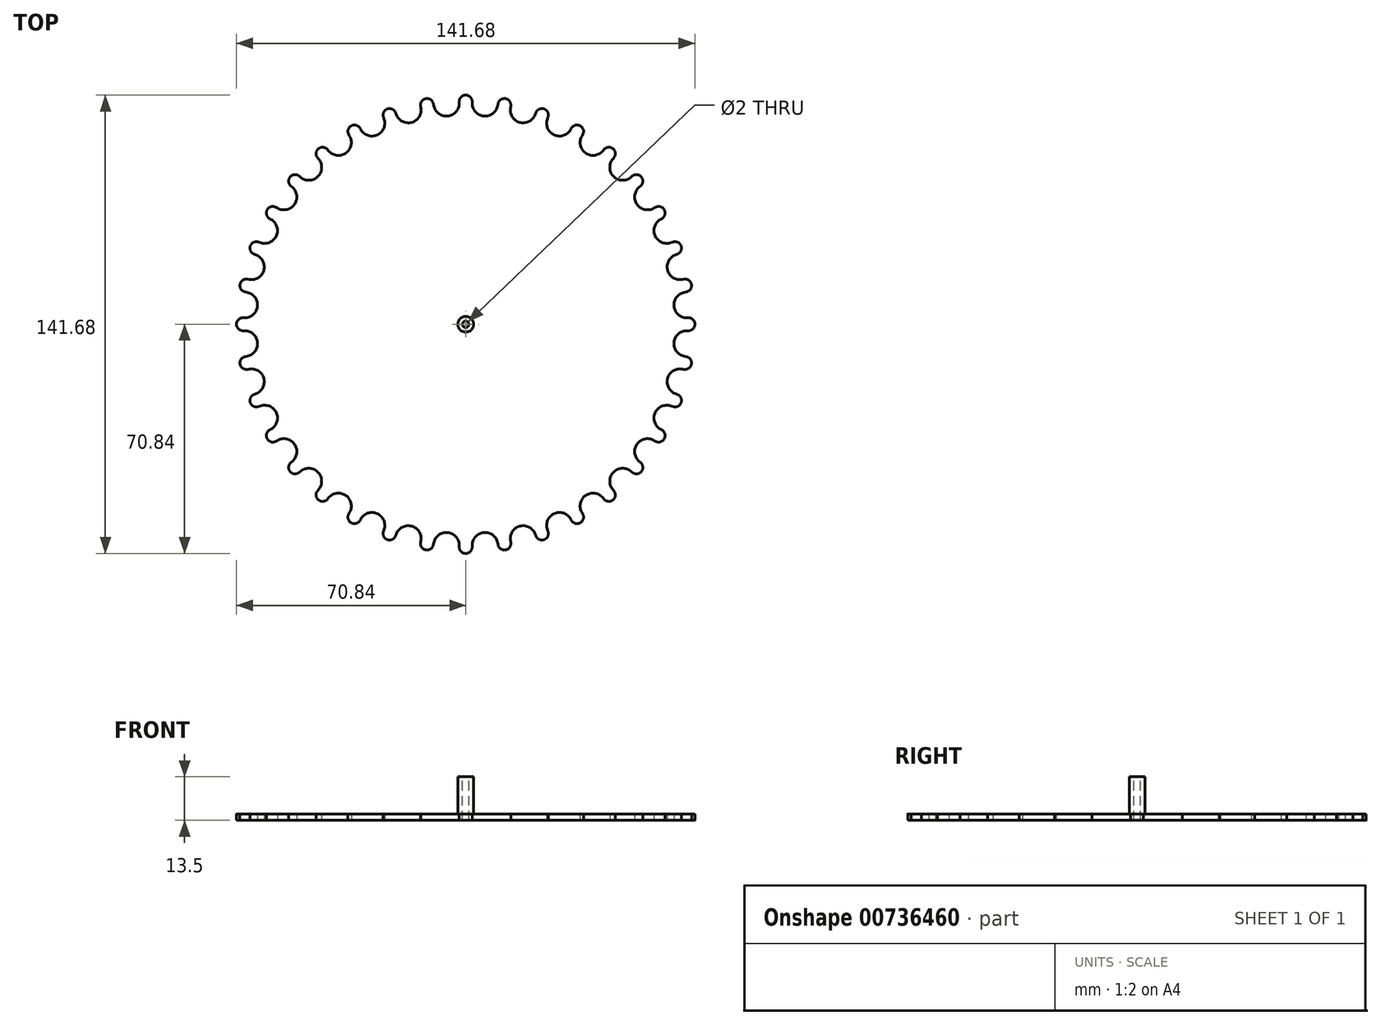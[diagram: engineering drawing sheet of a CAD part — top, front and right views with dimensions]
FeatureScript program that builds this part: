
annotation { "Feature Type Name" : "Feature", "Feature Type Description" : "" }
export const myFeature = defineFeature(function(context is Context, id is Id, definition is map)
    precondition{}
    {
        {
            var Q0;
            Q0=qCreatedBy(makeId("Top.planeOp"),FACE);
            var sketch = newSketch(context, id + "F0", { "sketchPlane" : qUnion([Q0])});
            skArc(sketch, "E0", {"start": v(2, 68.84) * mm, "mid": v(0, 70.84) * mm, "end": v(-2, 68.84) * mm});
            skLineSegment(sketch, "E1", {"start": v(2, 68.84) * mm, "end": v(2, 68.32) * mm});
            skLineSegment(sketch, "E2", {"start": v(-2, 68.84) * mm, "end": v(-2, 68.32) * mm});
            skLineSegment(sketch, "E3", {"start": v(-5.98, 68.32) * mm, "end": v(-5.63, 64.36) * mm, "construction": true});
            skArc(sketch, "E4", {"start": v(-5.63, 64.36) * mm, "mid": v(-3.04, 65.63) * mm, "end": v(-2, 68.32) * mm});
            skLineSegment(sketch, "E5", {"start": v(-5.63, 64.36) * mm, "end": v(-4.63, 64.44) * mm, "construction": true});
            skLineSegment(sketch, "E6", {"start": v(0, 0) * mm, "end": v(-5.63, 64.36) * mm});
            skArc(sketch, "E7", {"start": v(2, 68.32) * mm, "mid": v(3.04, 65.63) * mm, "end": v(5.63, 64.36) * mm});
            skLineSegment(sketch, "E8", {"start": v(5.98, 68.32) * mm, "end": v(5.63, 64.36) * mm, "construction": true});
            skLineSegment(sketch, "E9", {"start": v(5.63, 64.36) * mm, "end": v(4.63, 64.44) * mm, "construction": true});
            skLineSegment(sketch, "E10", {"start": v(0, 0) * mm, "end": v(5.63, 64.36) * mm});
            skCircle(sketch, "E11.cCircle", {"center": v(0, 0) * mm, "radius": 68.84 * mm, "construction": true});
            skLineSegment(sketch, "E11.0", {"start": v(0, 68.84) * mm, "end": v(11.95, 67.8) * mm, "construction": true});
            skLineSegment(sketch, "E11.1", {"start": v(11.95, 67.8) * mm, "end": v(23.55, 64.7) * mm, "construction": true});
            skLineSegment(sketch, "E11.2", {"start": v(23.55, 64.7) * mm, "end": v(34.42, 59.62) * mm, "construction": true});
            skLineSegment(sketch, "E11.3", {"start": v(34.42, 59.62) * mm, "end": v(44.25, 52.74) * mm, "construction": true});
            skLineSegment(sketch, "E11.4", {"start": v(44.25, 52.74) * mm, "end": v(52.74, 44.25) * mm, "construction": true});
            skLineSegment(sketch, "E11.5", {"start": v(52.74, 44.25) * mm, "end": v(59.62, 34.42) * mm, "construction": true});
            skLineSegment(sketch, "E11.6", {"start": v(59.62, 34.42) * mm, "end": v(64.7, 23.55) * mm, "construction": true});
            skLineSegment(sketch, "E11.7", {"start": v(64.7, 23.55) * mm, "end": v(67.8, 11.95) * mm, "construction": true});
            skLineSegment(sketch, "E11.8", {"start": v(67.8, 11.95) * mm, "end": v(68.84, 0) * mm, "construction": true});
            skLineSegment(sketch, "E11.9", {"start": v(68.84, 0) * mm, "end": v(67.8, -11.95) * mm, "construction": true});
            skLineSegment(sketch, "E11.10", {"start": v(67.8, -11.95) * mm, "end": v(64.7, -23.55) * mm, "construction": true});
            skLineSegment(sketch, "E11.11", {"start": v(64.7, -23.55) * mm, "end": v(59.62, -34.42) * mm, "construction": true});
            skLineSegment(sketch, "E11.12", {"start": v(59.62, -34.42) * mm, "end": v(52.74, -44.25) * mm, "construction": true});
            skLineSegment(sketch, "E11.13", {"start": v(52.74, -44.25) * mm, "end": v(44.25, -52.74) * mm, "construction": true});
            skLineSegment(sketch, "E11.14", {"start": v(44.25, -52.74) * mm, "end": v(34.42, -59.62) * mm, "construction": true});
            skLineSegment(sketch, "E11.15", {"start": v(34.42, -59.62) * mm, "end": v(23.55, -64.7) * mm, "construction": true});
            skLineSegment(sketch, "E11.16", {"start": v(23.55, -64.7) * mm, "end": v(11.95, -67.8) * mm, "construction": true});
            skLineSegment(sketch, "E11.17", {"start": v(11.95, -67.8) * mm, "end": v(0, -68.84) * mm, "construction": true});
            skLineSegment(sketch, "E11.18", {"start": v(0, -68.84) * mm, "end": v(-11.95, -67.8) * mm, "construction": true});
            skLineSegment(sketch, "E11.19", {"start": v(-11.95, -67.8) * mm, "end": v(-23.55, -64.7) * mm, "construction": true});
            skLineSegment(sketch, "E11.20", {"start": v(-23.55, -64.7) * mm, "end": v(-34.42, -59.62) * mm, "construction": true});
            skLineSegment(sketch, "E11.21", {"start": v(-34.42, -59.62) * mm, "end": v(-44.25, -52.74) * mm, "construction": true});
            skLineSegment(sketch, "E11.22", {"start": v(-44.25, -52.74) * mm, "end": v(-52.74, -44.25) * mm, "construction": true});
            skLineSegment(sketch, "E11.23", {"start": v(-52.74, -44.25) * mm, "end": v(-59.62, -34.42) * mm, "construction": true});
            skLineSegment(sketch, "E11.24", {"start": v(-59.62, -34.42) * mm, "end": v(-64.7, -23.55) * mm, "construction": true});
            skLineSegment(sketch, "E11.25", {"start": v(-64.7, -23.55) * mm, "end": v(-67.8, -11.95) * mm, "construction": true});
            skLineSegment(sketch, "E11.26", {"start": v(-67.8, -11.95) * mm, "end": v(-68.84, 0) * mm, "construction": true});
            skLineSegment(sketch, "E11.27", {"start": v(-68.84, 0) * mm, "end": v(-67.8, 11.95) * mm});
            skLineSegment(sketch, "E11.28", {"start": v(-67.8, 11.95) * mm, "end": v(-64.7, 23.55) * mm, "construction": true});
            skLineSegment(sketch, "E11.29", {"start": v(-64.7, 23.55) * mm, "end": v(-59.62, 34.42) * mm, "construction": true});
            skLineSegment(sketch, "E11.30", {"start": v(-59.62, 34.42) * mm, "end": v(-52.74, 44.25) * mm, "construction": true});
            skLineSegment(sketch, "E11.31", {"start": v(-52.74, 44.25) * mm, "end": v(-44.25, 52.74) * mm, "construction": true});
            skLineSegment(sketch, "E11.32", {"start": v(-44.25, 52.74) * mm, "end": v(-34.42, 59.62) * mm, "construction": true});
            skLineSegment(sketch, "E11.33", {"start": v(-34.42, 59.62) * mm, "end": v(-23.55, 64.7) * mm, "construction": true});
            skLineSegment(sketch, "E11.34", {"start": v(-23.55, 64.7) * mm, "end": v(-11.95, 67.8) * mm, "construction": true});
            skLineSegment(sketch, "E11.35", {"start": v(-11.95, 67.8) * mm, "end": v(0, 68.84) * mm, "construction": true});
            skSolve(sketch);
        }
        {
            var Q0;
            Q0=qSketchRegion(id+"F0",true);
            extrude(context, id + "F1", {"entities" : qUnion([Q0]), "endBound" : BoundingType.SYMMETRIC, "depth" : 2 * mm, "offsetDistance" : 25 * mm});
        }
        {
            var Q0;
            Q0=makeQuery(id+"F1.opExtrude","SWEPT_BODY",BODY,{"disambiguationData":[OSD([sQuery(id+"F0.wireOp",EDGE,"E0"),sQuery(id+"F0.wireOp",EDGE,"E1"),sQuery(id+"F0.wireOp",EDGE,"E2"),sQuery(id+"F0.wireOp",EDGE,"E4"),sQuery(id+"F0.wireOp",EDGE,"W5vAHDtY-rvEH-ViCa-0FPo-8mxshjeyYw7U"),sQuery(id+"F0.wireOp",EDGE,"J2sdAHte-avJF-ZFeu-cnuh-1Djj5LRI9oCG"),sQuery(id+"F0.wireOp",EDGE,"E6")])]});
            var Q1;
            Q1=makeQuery(id+"F1.opExtrude","SWEPT_EDGE",EDGE,{"disambiguationData":[OSD([sQuery(id+"F0.wireOp",EDGE,"E6"),sQuery(id+"F0.wireOp",EDGE,"E10")])]});
            circularPattern(context, id + "F2", {"operationType" : NewBodyOperationType.ADD, "entities" : qUnion([Q0]), "axis" : qUnion([Q1]), "angle" : 360 * degree, "instanceCount" : 36, "equalSpace" : true});
        }
        {
            var Q0;
            Q0=qCreatedBy(makeId("Top.planeOp"),FACE);
            var sketch = newSketch(context, id + "F3", { "sketchPlane" : qUnion([Q0])});
            skCircle(sketch, "E12", {"center": v(0, 0) * mm, "radius": 2.4 * mm});
            skSolve(sketch);
        }
        {
            var Q0;
            Q0=qSketchRegion(id+"F3",true);
            extrude(context, id + "F4", {"entities" : qUnion([Q0]), "operationType" : NewBodyOperationType.ADD, "depth" : 12.5 * mm, "offsetDistance" : 25 * mm});
        }
        {
            var Q0;
            Q0=makeQuery(id+"F4.opExtrude","CAP_FACE",FACE,{"disambiguationData":[OSD([sQuery(id+"F3.wireOp",EDGE,"E12")])],"isStart":false});
            var sketch = newSketch(context, id + "F5", { "sketchPlane" : qUnion([Q0])});
            skCircle(sketch, "E13", {"center": v(0, 0) * mm, "radius": 1 * mm});
            skSolve(sketch);
        }
        {
            var Q0;
            Q0=qSketchRegion(id+"F5",true);
            extrude(context, id + "F6", {"entities" : qUnion([Q0]), "operationType" : NewBodyOperationType.REMOVE, "endBound" : BoundingType.THROUGH_ALL, "oppositeDirection" : true, "depth" : 25 * mm, "offsetDistance" : 25 * mm});
        }
    });
